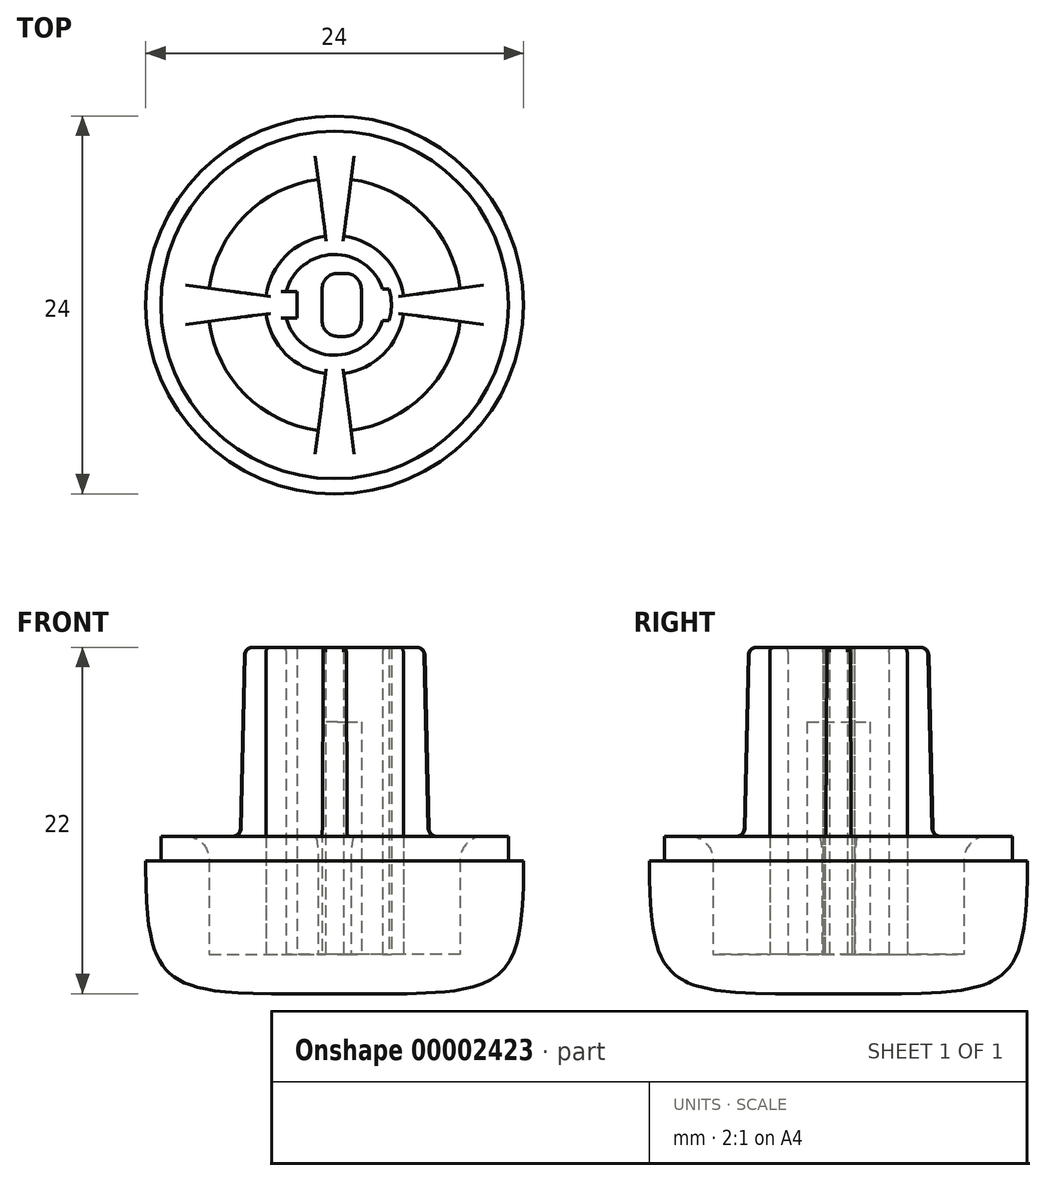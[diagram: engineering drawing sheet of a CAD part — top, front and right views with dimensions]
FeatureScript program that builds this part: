
annotation { "Feature Type Name" : "Feature", "Feature Type Description" : "" }
export const myFeature = defineFeature(function(context is Context, id is Id, definition is map)
    precondition{}
    {
        {
            var Q0;
            Q0=qCreatedBy(makeId("Front.planeOp"),FACE);
            var sketch = newSketch(context, id + "F0", { "sketchPlane" : qUnion([Q0])});
            skLineSegment(sketch, "E0", {"start": v(8.04, -7.5) * mm, "end": v(8.04, 0) * mm});
            skLineSegment(sketch, "E1", {"start": v(8.04, 0) * mm, "end": v(11.04, 0) * mm});
            skLineSegment(sketch, "E2", {"start": v(11.04, 0) * mm, "end": v(11.04, -1.56) * mm});
            skLineSegment(sketch, "E3", {"start": v(11.04, -1.56) * mm, "end": v(12, -1.56) * mm});
            skLineSegment(sketch, "E4", {"start": v(12, -1.56) * mm, "end": v(12, -10) * mm});
            skLineSegment(sketch, "E5", {"start": v(12, -10) * mm, "end": v(0, -10) * mm});
            skLineSegment(sketch, "E6", {"start": v(0, -10) * mm, "end": v(0, -7.5) * mm});
            skLineSegment(sketch, "E7", {"start": v(4.4, -7.5) * mm, "end": v(4.4, 12) * mm});
            skLineSegment(sketch, "E8", {"start": v(4.4, 12) * mm, "end": v(3.2, 12) * mm});
            skLineSegment(sketch, "E9", {"start": v(3.2, 12) * mm, "end": v(3.2, -7.5) * mm});
            skLineSegment(sketch, "E10", {"start": v(0, -7.5) * mm, "end": v(3.2, -7.5) * mm});
            skLineSegment(sketch, "E11", {"start": v(4.4, -7.5) * mm, "end": v(8.04, -7.5) * mm});
            skLineSegment(sketch, "E12", {"start": v(4.4, 12) * mm, "end": v(5.72, 12) * mm});
            skLineSegment(sketch, "E13", {"start": v(5.72, 12) * mm, "end": v(6, 0) * mm});
            skLineSegment(sketch, "E14", {"start": v(6, 0) * mm, "end": v(8.04, 0) * mm});
            skSolve(sketch);
        }
        {
            var Q0;
            Q0=makeQuery(id+"F0.imprint","IMPRINT",FACE,{"disambiguationData":[TD([[makeQuery(id+"F0.imprint","IMPRINT",EDGE,{"derivedFrom":sQuery(id+"F0.wireOp",EDGE,"E0")}),-1.0]])]});
            var Q1;
            Q1=sQuery(id+"F0.wireOp",EDGE,"E6");
            revolve(context, id + "F1", {"entities" : qUnion([Q0]), "axis" : qUnion([Q1]), "revolveType" : RevolveType.FULL});
        }
        {
            var Q0;
            Q0=makeQuery(id+"F1.opRevolve","SWEPT_EDGE",EDGE,{"disambiguationData":[OSD([sQuery(id+"F0.wireOp",EDGE,"E0"),sQuery(id+"F0.wireOp",EDGE,"E1"),sQuery(id+"F0.wireOp",EDGE,"E14")])]});
            fillet(context, id + "F2", {"entities" : qUnion([Q0]), "radius" : 1.5 * mm, "tangentPropagation" : true, "allowEdgeOverflow" : false});
        }
        {
            var Q0;
            Q0=makeQuery(id+"F0.imprint","IMPRINT",FACE,{"disambiguationData":[TD([[makeQuery(id+"F0.imprint","IMPRINT",EDGE,{"derivedFrom":sQuery(id+"F0.wireOp",EDGE,"E0")}),-1.0]])]});
            var Q1;
            Q1=makeQuery(id+"F0.imprint","IMPRINT",FACE,{"disambiguationData":[TD([[makeQuery(id+"F0.imprint","IMPRINT",EDGE,{"derivedFrom":sQuery(id+"F0.wireOp",EDGE,"E0")}),1.0]])]});
            var Q2;
            Q2=sQuery(id+"F0.wireOp",EDGE,"E6");
            revolve(context, id + "F3", {"entities" : qUnion([Q0, Q1]), "axis" : qUnion([Q2]), "revolveType" : RevolveType.SYMMETRIC, "angle" : 15 * degree});
        }
        {
            var Q0;
            Q0=makeQuery(id+"F3.opRevolve","SWEPT_EDGE",EDGE,{"disambiguationData":[OSD([sQuery(id+"F0.wireOp",EDGE,"E12"),sQuery(id+"F0.wireOp",EDGE,"E13")])]});
            var Q1;
            Q1=makeQuery(id+"F3.opRevolve","SWEPT_EDGE",EDGE,{"disambiguationData":[OSD([sQuery(id+"F0.wireOp",EDGE,"E13"),sQuery(id+"F0.wireOp",EDGE,"E14")])]});
            fillet(context, id + "F4", {"entities" : qUnion([Q0, Q1]), "radius" : 0.5 * mm, "tangentPropagation" : true, "allowEdgeOverflow" : false});
        }
        {
            var Q0;
            Q0=makeQuery(id+"F3.opRevolve","SWEPT_BODY",BODY,{"disambiguationData":[OSD([sQuery(id+"F0.wireOp",EDGE,"E0"),sQuery(id+"F0.wireOp",EDGE,"E7"),sQuery(id+"F0.wireOp",EDGE,"E11"),sQuery(id+"F0.wireOp",EDGE,"E12"),sQuery(id+"F0.wireOp",EDGE,"E13"),sQuery(id+"F0.wireOp",EDGE,"E14")])]});
            var Q1;
            Q1=sQuery(id+"F0.wireOp",EDGE,"E6");
            circularPattern(context, id + "F5", {"entities" : qUnion([Q0]), "axis" : qUnion([Q1]), "angle" : 90 * degree, "instanceCount" : 4});
        }
        {
            var Q0;
            Q0=makeQuery(id+"F1.opRevolve","SWEPT_BODY",BODY,{"disambiguationData":[OSD([sQuery(id+"F0.wireOp",EDGE,"E0"),sQuery(id+"F0.wireOp",EDGE,"E1"),sQuery(id+"F0.wireOp",EDGE,"E2"),sQuery(id+"F0.wireOp",EDGE,"E3"),sQuery(id+"F0.wireOp",EDGE,"E4"),sQuery(id+"F0.wireOp",EDGE,"E5"),sQuery(id+"F0.wireOp",EDGE,"E6"),sQuery(id+"F0.wireOp",EDGE,"E7"),sQuery(id+"F0.wireOp",EDGE,"E8"),sQuery(id+"F0.wireOp",EDGE,"E9"),sQuery(id+"F0.wireOp",EDGE,"E10"),sQuery(id+"F0.wireOp",EDGE,"E11")])]});
            var Q1;
            Q1=makeQuery(id+"F3.opRevolve","SWEPT_BODY",BODY,{"disambiguationData":[OSD([sQuery(id+"F0.wireOp",EDGE,"E1"),sQuery(id+"F0.wireOp",EDGE,"E2"),sQuery(id+"F0.wireOp",EDGE,"E3"),sQuery(id+"F0.wireOp",EDGE,"E4"),sQuery(id+"F0.wireOp",EDGE,"E5"),sQuery(id+"F0.wireOp",EDGE,"E6"),sQuery(id+"F0.wireOp",EDGE,"E8"),sQuery(id+"F0.wireOp",EDGE,"E9"),sQuery(id+"F0.wireOp",EDGE,"E10"),sQuery(id+"F0.wireOp",EDGE,"E12"),sQuery(id+"F0.wireOp",EDGE,"E13"),sQuery(id+"F0.wireOp",EDGE,"E14")])]});
            var Q2;
            Q2=makeQuery(id+"F5.opPattern","COPY",BODY,{"derivedFrom":makeQuery(id+"F3.opRevolve","SWEPT_BODY",BODY,{"disambiguationData":[OSD([sQuery(id+"F0.wireOp",EDGE,"E1"),sQuery(id+"F0.wireOp",EDGE,"E2"),sQuery(id+"F0.wireOp",EDGE,"E3"),sQuery(id+"F0.wireOp",EDGE,"E4"),sQuery(id+"F0.wireOp",EDGE,"E5"),sQuery(id+"F0.wireOp",EDGE,"E6"),sQuery(id+"F0.wireOp",EDGE,"E8"),sQuery(id+"F0.wireOp",EDGE,"E9"),sQuery(id+"F0.wireOp",EDGE,"E10"),sQuery(id+"F0.wireOp",EDGE,"E12"),sQuery(id+"F0.wireOp",EDGE,"E13"),sQuery(id+"F0.wireOp",EDGE,"E14")])]}),"instanceName":"2"});
            var Q3;
            Q3=makeQuery(id+"F5.opPattern","COPY",BODY,{"derivedFrom":makeQuery(id+"F3.opRevolve","SWEPT_BODY",BODY,{"disambiguationData":[OSD([sQuery(id+"F0.wireOp",EDGE,"E1"),sQuery(id+"F0.wireOp",EDGE,"E2"),sQuery(id+"F0.wireOp",EDGE,"E3"),sQuery(id+"F0.wireOp",EDGE,"E4"),sQuery(id+"F0.wireOp",EDGE,"E5"),sQuery(id+"F0.wireOp",EDGE,"E6"),sQuery(id+"F0.wireOp",EDGE,"E8"),sQuery(id+"F0.wireOp",EDGE,"E9"),sQuery(id+"F0.wireOp",EDGE,"E10"),sQuery(id+"F0.wireOp",EDGE,"E12"),sQuery(id+"F0.wireOp",EDGE,"E13"),sQuery(id+"F0.wireOp",EDGE,"E14")])]}),"instanceName":"1"});
            var Q4;
            Q4=makeQuery(id+"F5.opPattern","COPY",BODY,{"derivedFrom":makeQuery(id+"F3.opRevolve","SWEPT_BODY",BODY,{"disambiguationData":[OSD([sQuery(id+"F0.wireOp",EDGE,"E1"),sQuery(id+"F0.wireOp",EDGE,"E2"),sQuery(id+"F0.wireOp",EDGE,"E3"),sQuery(id+"F0.wireOp",EDGE,"E4"),sQuery(id+"F0.wireOp",EDGE,"E5"),sQuery(id+"F0.wireOp",EDGE,"E6"),sQuery(id+"F0.wireOp",EDGE,"E8"),sQuery(id+"F0.wireOp",EDGE,"E9"),sQuery(id+"F0.wireOp",EDGE,"E10"),sQuery(id+"F0.wireOp",EDGE,"E12"),sQuery(id+"F0.wireOp",EDGE,"E13"),sQuery(id+"F0.wireOp",EDGE,"E14")])]}),"instanceName":"3"});
            booleanBodies(context, id + "F6", {"operationType" : BooleanOperationType.UNION, "tools" : qUnion([Q0, Q1, Q2, Q3, Q4])});
        }
        {
            var Q0;
            Q0=makeQuery(id+"F1.opRevolve","SWEPT_EDGE",EDGE,{"disambiguationData":[OSD([sQuery(id+"F0.wireOp",EDGE,"E4"),sQuery(id+"F0.wireOp",EDGE,"E5")])]});
            fillet(context, id + "F7", {"entities" : qUnion([Q0]), "radius" : 8 * mm, "tangentPropagation" : true, "rho" : 0.65, "crossSection" : FilletCrossSection.CONIC, "allowEdgeOverflow" : false});
        }
        {
            var Q0;
            Q0=makeQuery(id+"F1.opRevolve","SWEPT_FACE",FACE,{"disambiguationData":[OSD([sQuery(id+"F0.wireOp",EDGE,"E10")])]});
            var sketch = newSketch(context, id + "F8", { "sketchPlane" : qUnion([Q0])});
            skLineSegment(sketch, "E15.bottom", {"start": v(-0.8, -2) * mm, "end": v(1.7, -2) * mm});
            skLineSegment(sketch, "E15.top", {"start": v(-0.8, 2) * mm, "end": v(1.7, 2) * mm});
            skLineSegment(sketch, "E15.left", {"start": v(-0.8, -2) * mm, "end": v(-0.8, 2) * mm});
            skLineSegment(sketch, "E15.right", {"start": v(1.7, -2) * mm, "end": v(1.7, 2) * mm});
            skPoint(sketch, "E16", {"position": v(-0.8, 0) * mm});
            skLineSegment(sketch, "E17", {"start": v(-3.09, 0.85) * mm, "end": v(-2.4, 0.85) * mm});
            skLineSegment(sketch, "E18", {"start": v(-2.4, 0.85) * mm, "end": v(-2.4, -0.85) * mm});
            skLineSegment(sketch, "E19", {"start": v(-2.4, -0.85) * mm, "end": v(-3.09, -0.85) * mm});
            skArc(sketch, "E20", {"start": v(-3.09, 0.85) * mm, "mid": v(-3.2, 0) * mm, "end": v(-3.09, -0.85) * mm});
            skPoint(sketch, "E21", {"position": v(-2.4, 0) * mm});
            skLineSegment(sketch, "E22", {"start": v(-2.4, 0) * mm, "end": v(-3.2, 0) * mm, "construction": true});
            skArc(sketch, "E23", {"start": v(3.46, -1) * mm, "mid": v(3.6, 0) * mm, "end": v(3.46, 1) * mm});
            skLineSegment(sketch, "E24", {"start": v(3.46, 1) * mm, "end": v(3.04, 1) * mm});
            skLineSegment(sketch, "E25", {"start": v(3.04, 1) * mm, "end": v(3.04, -1) * mm});
            skLineSegment(sketch, "E26", {"start": v(3.04, -1) * mm, "end": v(3.46, -1) * mm});
            skPoint(sketch, "E27", {"position": v(3.04, 0) * mm});
            skPoint(sketch, "E28", {"position": v(3.6, 0) * mm});
            skSolve(sketch);
        }
        {
            var Q0;
            {var subQ0=sQuery(id+"F0.wireOp",EDGE,"E8");var subQ1=makeQuery(id+"F3.opRevolve","SWEPT_FACE",FACE,{"disambiguationData":[OSD([subQ0,sQuery(id+"F0.wireOp",EDGE,"E12")])]});Q0=makeQuery(id+"F6.opBoolean","MERGE",FACE,{"derivedFrom":[makeQuery(id+"F1.opRevolve","SWEPT_FACE",FACE,{"disambiguationData":[OSD([subQ0])]}),subQ1,makeQuery(id+"F5.opPattern","COPY",FACE,{"derivedFrom":subQ1,"instanceName":"1"}),makeQuery(id+"F5.opPattern","COPY",FACE,{"derivedFrom":subQ1,"instanceName":"2"}),makeQuery(id+"F5.opPattern","COPY",FACE,{"derivedFrom":subQ1,"instanceName":"3"})]});}
            cPlane(context, id + "F9", {"entities" : qUnion([Q0]), "cplaneType" : CPlaneType.OFFSET, "offset" : 4.73 * mm, "oppositeDirection" : true, "width" : 150 * mm, "height" : 150 * mm});
        }
        {
            var Q0;
            Q0=makeQuery(id+"F8.imprint","IMPRINT",FACE,{"disambiguationData":[TD([[makeQuery(id+"F8.imprint","IMPRINT",EDGE,{"derivedFrom":sQuery(id+"F8.wireOp",EDGE,"E15.bottom")}),1.0]])]});
            var Q1;
            Q1=qCreatedBy(id+"F9.planeOp",FACE);
            extrude(context, id + "F10", {"entities" : qUnion([Q0]), "operationType" : NewBodyOperationType.ADD, "endBound" : BoundingType.UP_TO_SURFACE, "endBoundEntityFace" : qUnion([Q1]), "depth" : 12 * mm});
        }
        {
            var Q0;
            Q0=makeQuery(id+"F8.imprint","IMPRINT",FACE,{"disambiguationData":[TD([[makeQuery(id+"F8.imprint","IMPRINT",EDGE,{"derivedFrom":sQuery(id+"F8.wireOp",EDGE,"E17")}),-1.0]])]});
            var Q1;
            {var subQ0=sQuery(id+"F0.wireOp",EDGE,"E8");var subQ1=makeQuery(id+"F3.opRevolve","SWEPT_FACE",FACE,{"disambiguationData":[OSD([subQ0,sQuery(id+"F0.wireOp",EDGE,"E12")])]});Q1=makeQuery(id+"F6.opBoolean","MERGE",FACE,{"derivedFrom":[makeQuery(id+"F1.opRevolve","SWEPT_FACE",FACE,{"disambiguationData":[OSD([subQ0])]}),subQ1,makeQuery(id+"F5.opPattern","COPY",FACE,{"derivedFrom":subQ1,"instanceName":"1"}),makeQuery(id+"F5.opPattern","COPY",FACE,{"derivedFrom":subQ1,"instanceName":"2"}),makeQuery(id+"F5.opPattern","COPY",FACE,{"derivedFrom":subQ1,"instanceName":"3"})]});}
            extrude(context, id + "F11", {"entities" : qUnion([Q0]), "operationType" : NewBodyOperationType.ADD, "endBound" : BoundingType.UP_TO_SURFACE, "endBoundEntityFace" : qUnion([Q1]), "depth" : 25 * mm});
        }
        {
            var Q0;
            Q0=makeQuery(id+"F8.imprint","IMPRINT",FACE,{"disambiguationData":[TD([[makeQuery(id+"F8.imprint","IMPRINT",EDGE,{"derivedFrom":sQuery(id+"F8.wireOp",EDGE,"E23")}),1.0]])]});
            var Q1;
            {var subQ0=sQuery(id+"F0.wireOp",EDGE,"E12");var subQ1=sQuery(id+"F0.wireOp",EDGE,"E8");var subQ2=makeQuery(id+"F3.opRevolve","SWEPT_FACE",FACE,{"disambiguationData":[OSD([subQ1,subQ0])]});Q1=makeQuery(id+"F11.boolean.opBoolean","MERGE",FACE,{"derivedFrom":[makeQuery(id+"F6.opBoolean","MERGE",FACE,{"derivedFrom":[makeQuery(id+"F1.opRevolve","SWEPT_FACE",FACE,{"disambiguationData":[OSD([subQ1])]}),subQ2,makeQuery(id+"F5.opPattern","COPY",FACE,{"derivedFrom":subQ2,"instanceName":"1"}),makeQuery(id+"F5.opPattern","COPY",FACE,{"derivedFrom":subQ2,"instanceName":"2"}),makeQuery(id+"F5.opPattern","COPY",FACE,{"derivedFrom":subQ2,"instanceName":"3"})]}),makeQuery(id+"F11.opExtrude","CAP_FACE",FACE,{"disambiguationData":[OSD([subQ1,subQ0])],"isStart":false})]});}
            extrude(context, id + "F12", {"entities" : qUnion([Q0]), "operationType" : NewBodyOperationType.REMOVE, "endBound" : BoundingType.UP_TO_SURFACE, "endBoundEntityFace" : qUnion([Q1]), "depth" : 25 * mm});
        }
        {
            var Q0;
            Q0=makeQuery(id+"F10.opExtrude","SWEPT_EDGE",EDGE,{"disambiguationData":[OSD([sQuery(id+"F8.wireOp",EDGE,"E15.top"),sQuery(id+"F8.wireOp",EDGE,"E15.left")])]});
            var Q1;
            Q1=makeQuery(id+"F10.opExtrude","SWEPT_EDGE",EDGE,{"disambiguationData":[OSD([sQuery(id+"F8.wireOp",EDGE,"E15.bottom"),sQuery(id+"F8.wireOp",EDGE,"E15.left")])]});
            var Q2;
            Q2=makeQuery(id+"F10.opExtrude","SWEPT_EDGE",EDGE,{"disambiguationData":[OSD([sQuery(id+"F8.wireOp",EDGE,"E15.top"),sQuery(id+"F8.wireOp",EDGE,"E15.right")])]});
            var Q3;
            Q3=makeQuery(id+"F10.opExtrude","SWEPT_EDGE",EDGE,{"disambiguationData":[OSD([sQuery(id+"F8.wireOp",EDGE,"E15.bottom"),sQuery(id+"F8.wireOp",EDGE,"E15.right")])]});
            fillet(context, id + "F13", {"entities" : qUnion([Q0, Q1, Q2, Q3]), "radius" : 1 * mm, "tangentPropagation" : true, "allowEdgeOverflow" : false});
        }
        {
            var Q0;
            {var subQ0=sQuery(id+"F0.wireOp",EDGE,"E7");var subQ1=sQuery(id+"F0.wireOp",EDGE,"E8");var subQ2=sQuery(id+"F0.wireOp",EDGE,"E12");var subQ5=sQuery(id+"F0.wireOp",EDGE,"E1");var subQ6=sQuery(id+"F0.wireOp",EDGE,"E2");var subQ7=sQuery(id+"F0.wireOp",EDGE,"E3");var subQ8=sQuery(id+"F0.wireOp",EDGE,"E4");var subQ9=sQuery(id+"F0.wireOp",EDGE,"E5");var subQ10=sQuery(id+"F0.wireOp",EDGE,"E6");var subQ11=sQuery(id+"F0.wireOp",EDGE,"E9");var subQ12=sQuery(id+"F0.wireOp",EDGE,"E10");var subQ13=sQuery(id+"F0.wireOp",EDGE,"E13");var subQ14=sQuery(id+"F0.wireOp",EDGE,"E14");Q0=makeQuery(id+"F6.opBoolean","SPLIT",EDGE,{"disambiguationData":[TD([makeQuery(id+"F5.opPattern","COPY",FACE,{"derivedFrom":makeQuery(id+"F3.opRevolve","CAP_FACE",FACE,{"disambiguationData":[OSD([subQ5,subQ6,subQ7,subQ8,subQ9,subQ10,subQ1,subQ11,subQ12,subQ2,subQ13,subQ14])],"isStart":false}),"instanceName":"2"})])],"derivedFrom":makeQuery(id+"F1.opRevolve","SWEPT_EDGE",EDGE,{"disambiguationData":[OSD([subQ0,subQ1,subQ2])]})});}
            var Q1;
            {var subQ0=sQuery(id+"F0.wireOp",EDGE,"E7");var subQ1=sQuery(id+"F0.wireOp",EDGE,"E8");var subQ2=sQuery(id+"F0.wireOp",EDGE,"E12");var subQ5=sQuery(id+"F0.wireOp",EDGE,"E1");var subQ6=sQuery(id+"F0.wireOp",EDGE,"E2");var subQ7=sQuery(id+"F0.wireOp",EDGE,"E3");var subQ8=sQuery(id+"F0.wireOp",EDGE,"E4");var subQ9=sQuery(id+"F0.wireOp",EDGE,"E5");var subQ10=sQuery(id+"F0.wireOp",EDGE,"E6");var subQ11=sQuery(id+"F0.wireOp",EDGE,"E9");var subQ12=sQuery(id+"F0.wireOp",EDGE,"E10");var subQ13=sQuery(id+"F0.wireOp",EDGE,"E13");var subQ14=sQuery(id+"F0.wireOp",EDGE,"E14");Q1=makeQuery(id+"F6.opBoolean","SPLIT",EDGE,{"disambiguationData":[TD([makeQuery(id+"F3.opRevolve","CAP_FACE",FACE,{"disambiguationData":[OSD([subQ5,subQ6,subQ7,subQ8,subQ9,subQ10,subQ1,subQ11,subQ12,subQ2,subQ13,subQ14])],"isStart":true})])],"derivedFrom":makeQuery(id+"F1.opRevolve","SWEPT_EDGE",EDGE,{"disambiguationData":[OSD([subQ0,subQ1,subQ2])]})});}
            var Q2;
            {var subQ0=sQuery(id+"F0.wireOp",EDGE,"E7");var subQ1=sQuery(id+"F0.wireOp",EDGE,"E8");var subQ2=sQuery(id+"F0.wireOp",EDGE,"E12");var subQ5=sQuery(id+"F0.wireOp",EDGE,"E1");var subQ6=sQuery(id+"F0.wireOp",EDGE,"E2");var subQ7=sQuery(id+"F0.wireOp",EDGE,"E3");var subQ8=sQuery(id+"F0.wireOp",EDGE,"E4");var subQ9=sQuery(id+"F0.wireOp",EDGE,"E5");var subQ10=sQuery(id+"F0.wireOp",EDGE,"E6");var subQ11=sQuery(id+"F0.wireOp",EDGE,"E9");var subQ12=sQuery(id+"F0.wireOp",EDGE,"E10");var subQ13=sQuery(id+"F0.wireOp",EDGE,"E13");var subQ14=sQuery(id+"F0.wireOp",EDGE,"E14");Q2=makeQuery(id+"F6.opBoolean","SPLIT",EDGE,{"disambiguationData":[TD([makeQuery(id+"F3.opRevolve","CAP_FACE",FACE,{"disambiguationData":[OSD([subQ5,subQ6,subQ7,subQ8,subQ9,subQ10,subQ1,subQ11,subQ12,subQ2,subQ13,subQ14])],"isStart":false})])],"derivedFrom":makeQuery(id+"F1.opRevolve","SWEPT_EDGE",EDGE,{"disambiguationData":[OSD([subQ0,subQ1,subQ2])]})});}
            var Q3;
            {var subQ0=sQuery(id+"F0.wireOp",EDGE,"E7");var subQ1=sQuery(id+"F0.wireOp",EDGE,"E8");var subQ2=sQuery(id+"F0.wireOp",EDGE,"E12");var subQ5=sQuery(id+"F0.wireOp",EDGE,"E1");var subQ6=sQuery(id+"F0.wireOp",EDGE,"E2");var subQ7=sQuery(id+"F0.wireOp",EDGE,"E3");var subQ8=sQuery(id+"F0.wireOp",EDGE,"E4");var subQ9=sQuery(id+"F0.wireOp",EDGE,"E5");var subQ10=sQuery(id+"F0.wireOp",EDGE,"E6");var subQ11=sQuery(id+"F0.wireOp",EDGE,"E9");var subQ12=sQuery(id+"F0.wireOp",EDGE,"E10");var subQ13=sQuery(id+"F0.wireOp",EDGE,"E13");var subQ14=sQuery(id+"F0.wireOp",EDGE,"E14");Q3=makeQuery(id+"F6.opBoolean","SPLIT",EDGE,{"disambiguationData":[TD([makeQuery(id+"F5.opPattern","COPY",FACE,{"derivedFrom":makeQuery(id+"F3.opRevolve","CAP_FACE",FACE,{"disambiguationData":[OSD([subQ5,subQ6,subQ7,subQ8,subQ9,subQ10,subQ1,subQ11,subQ12,subQ2,subQ13,subQ14])],"isStart":false}),"instanceName":"1"})])],"derivedFrom":makeQuery(id+"F1.opRevolve","SWEPT_EDGE",EDGE,{"disambiguationData":[OSD([subQ0,subQ1,subQ2])]})});}
            var Q4;
            {var subQ1=sQuery(id+"F0.wireOp",EDGE,"E8");var subQ4=sQuery(id+"F0.wireOp",EDGE,"E9");Q4=makeQuery(id+"F12.boolean.opBoolean","SPLIT",EDGE,{"disambiguationData":[TD([makeQuery(id+"F11.opExtrude","SWEPT_FACE",FACE,{"disambiguationData":[OSD([sQuery(id+"F8.wireOp",EDGE,"E17")])]})])],"derivedFrom":makeQuery(id+"F1.opRevolve","SWEPT_EDGE",EDGE,{"disambiguationData":[OSD([subQ1,subQ4])]})});}
            var Q5;
            {var subQ1=sQuery(id+"F0.wireOp",EDGE,"E8");var subQ4=sQuery(id+"F0.wireOp",EDGE,"E9");Q5=makeQuery(id+"F12.boolean.opBoolean","SPLIT",EDGE,{"disambiguationData":[TD([makeQuery(id+"F11.opExtrude","SWEPT_FACE",FACE,{"disambiguationData":[OSD([sQuery(id+"F8.wireOp",EDGE,"E19")])]})])],"derivedFrom":makeQuery(id+"F1.opRevolve","SWEPT_EDGE",EDGE,{"disambiguationData":[OSD([subQ1,subQ4])]})});}
            fillet(context, id + "F14", {"entities" : qUnion([Q0, Q1, Q2, Q3, Q4, Q5]), "radius" : 0.3 * mm, "tangentPropagation" : true, "allowEdgeOverflow" : false});
        }
    });
